# Revit family: Qf_Summit_MDR245SS_Built_in_Drawer_Microwave_oven
name_source: partatom
category: Specialty Equipment
units: mm (PartAtom-declared; Revit-internal decimal feet)

## family parameters
Always vertical = Yes
Cut with Voids When Loaded = No
Part Type = Normal
Room Calculation Point = No
Round Connector Dimension = Use Diameter
Shared = No
Work Plane-Based = No

## types (1)
- Qf_Summit_MDR245SS_Built_in_Drawer_Microwave_oven
    Apparent Power = 1380 VA
    Conn Conduit = Yes
    Cycle = 60 Hz
    Default Elevation = 0"
    Depth = 23 1/4"
    Description = 24" Wide Built-In Drawer Microwave
    Elec Conn Connection Height = 0"
    Elec Conn RI Height = 0"
    FL Amps = 12 A
    Foodservice Equipment Identifier = Yes
    Height = 14 7/8"
    Identify Quantity as Lot = Yes
    Length = 23 1/2"
    Manufacturer = Summit
    Max Overcurrent Protection = 0 A
    Min Ckt Ampacity = 0 A
    Model = MDR245SS
    Number of Poles = 1
    Phase = 1
    Volts = 115 V
    Watts = 1380 W
    Weight in Pounds = 41

## geometry (parser evidence)
native form markers: Sweep x2
no freeform markers — native parametric forms only
